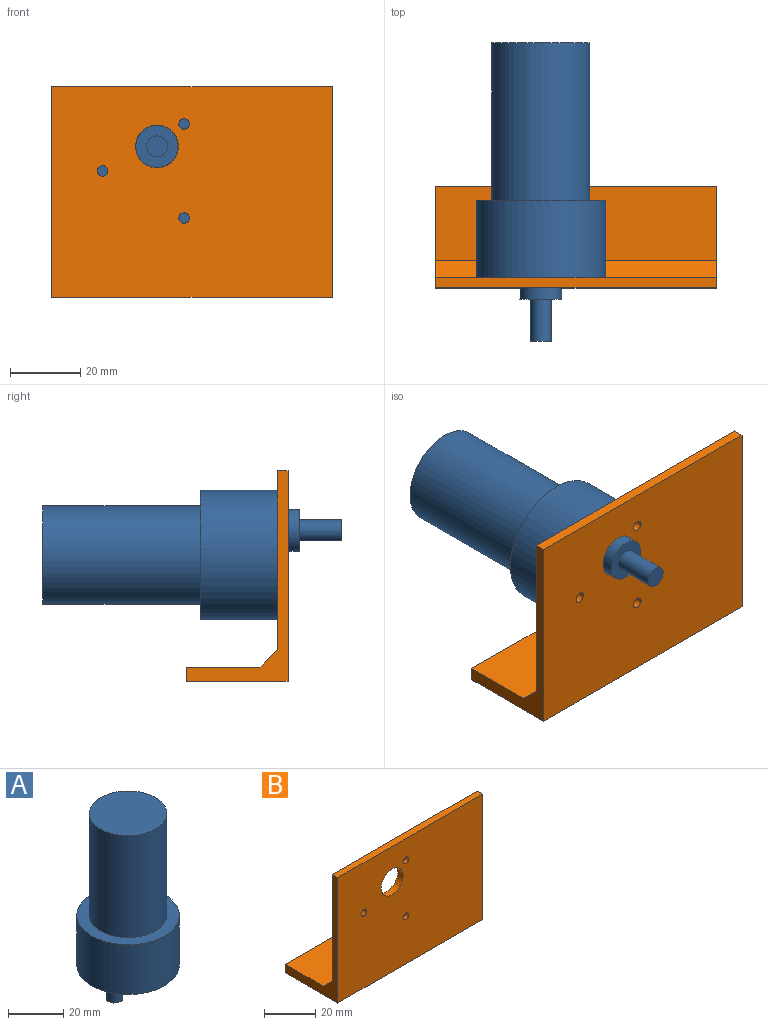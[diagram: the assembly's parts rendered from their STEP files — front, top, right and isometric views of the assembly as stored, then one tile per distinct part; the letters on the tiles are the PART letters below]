
ASSEMBLY  parts=2 mates=1
PART A: 15 faces, bbox 37x37x85.2 mm
  f0: cylinder r=18.5mm len=37mm, axis (0,0,-1), area 2557.3mm2, adj f1,f2
  f1: plane 37x37mm, normal (0,0,1), area 459.5mm2, adj f0,f3
  f2: plane 37x37mm, normal (0,0,-1), area 940.9mm2, adj f0,f5,f9,f11,f13
  f3: cylinder r=14mm len=45mm, axis (0,0,-1), area 3958.4mm2, adj f1,f4
  f4: plane 28x28mm, normal (0,0,1), area 615.8mm2, adj f3
  f5: cylinder r=6mm len=12mm, axis (0,0,1), area 233.7mm2, adj f2,f6
  f6: plane 12x12mm, normal (0,0,-1), area 84.8mm2, adj f5,f7
  f7: cylinder r=3mm len=12mm, axis (0,0,1), area 226.2mm2, adj f6,f8
  f8: plane 6x6mm, normal (0,0,-1), area 28.3mm2, adj f7
  f9: cylinder r=1.5mm len=5mm, axis (0,0,-1), area 47.1mm2, adj f2,f10
  f10: plane 3x3mm, normal (0,0,-1), area 7.1mm2, adj f9
  f11: cylinder r=1.5mm len=5mm, axis (0,0,-1), area 47.1mm2, adj f2,f12
  f12: plane 3x3mm, normal (0,0,-1), area 7.1mm2, adj f11
  f13: cylinder r=1.5mm len=5mm, axis (0,0,-1), area 47.1mm2, adj f2,f14
  f14: plane 3x3mm, normal (0,0,-1), area 7.1mm2, adj f13
PART B: 13 faces, bbox 80x29x60 mm
  f0: plane 80x3mm, normal (0,0,1), area 240mm2, adj f1,f3,f4,f5
  f1: plane 60x29mm, normal (-1,0,0), area 296.5mm2, adj f0,f2,f4,f5,f10,f11,f12
  f2: plane 80x29mm, normal (0,0,-1), area 2320mm2, adj f1,f3,f4,f11
  f3: plane 60x29mm, normal (1,0,0), area 296.5mm2, adj f0,f2,f4,f5,f10,f11,f12
  f4: plane 80x60mm, normal (0,-1,0), area 4661.9mm2, adj f0,f1,f2,f3,f6,f7,f8,f9
  f5: plane 80x51mm, normal (0,1,0), area 3941.9mm2, adj f0,f1,f3,f6,f7,f8,f9,f12
  f6: cylinder r=6.1mm len=12.2mm, axis (0,1,0), area 115mm2, adj f4,f5
  f7: cylinder r=1.5mm len=3mm, axis (0,1,0), area 28.3mm2, adj f4,f5
  f8: cylinder r=1.5mm len=3mm, axis (0,1,0), area 28.3mm2, adj f4,f5
  f9: cylinder r=1.5mm len=3mm, axis (0,1,0), area 28.3mm2, adj f4,f5
  f10: plane 80x21mm, normal (0,0,1), area 1680mm2, adj f1,f3,f11,f12
  f11: plane 80x4mm, normal (0,1,0), area 320mm2, adj f1,f2,f3,f10
  f12: plane 80x5mm, normal (0,0.71,0.71), area 565.7mm2, adj f1,f3,f5,f10
PLACE A rot(axis=(0,-0.71,-0.71),180deg) t=(-31.62,-5.01,15.72)mm
PLACE B t=(-31.62,-5.01,15.72)mm
MATE fastened A.f13 <-> B.f9  axis (0,-1,0) through (-23.87,-5.01,29.14)mm
